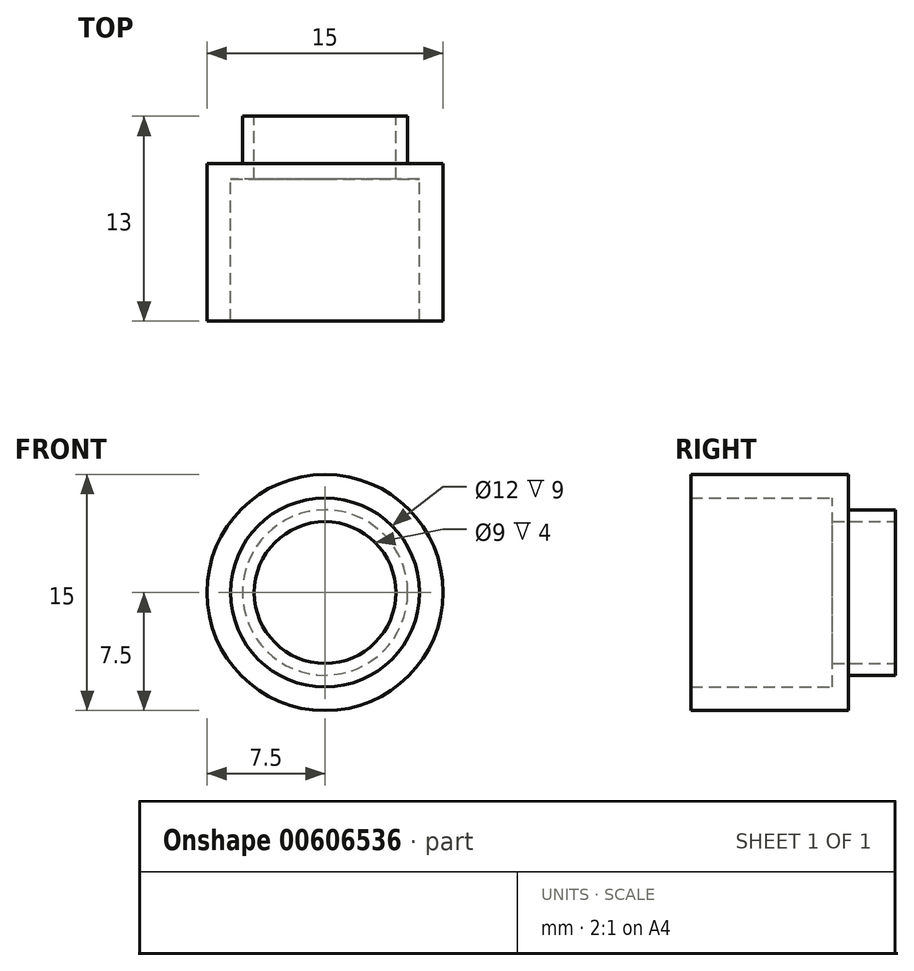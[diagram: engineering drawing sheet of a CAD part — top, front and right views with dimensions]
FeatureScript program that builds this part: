
annotation { "Feature Type Name" : "Feature", "Feature Type Description" : "" }
export const myFeature = defineFeature(function(context is Context, id is Id, definition is map)
    precondition{}
    {
        {
            var Q0;
            Q0=qCreatedBy(makeId("Front.planeOp"),FACE);
            var sketch = newSketch(context, id + "F0", { "sketchPlane" : qUnion([Q0])});
            skCircle(sketch, "E0", {"center": v(0, 0) * mm, "radius": 7.5 * mm});
            skCircle(sketch, "E1", {"center": v(0, 0) * mm, "radius": 6 * mm});
            skCircle(sketch, "E2", {"center": v(0, 0) * mm, "radius": 4.5 * mm});
            skCircle(sketch, "E3", {"center": v(0, 0) * mm, "radius": 5.25 * mm});
            skSolve(sketch);
        }
        {
            var Q0;
            Q0=makeQuery(id+"F0.imprint","IMPRINT",FACE,{"disambiguationData":[TD([[makeQuery(id+"F0.imprint","IMPRINT",EDGE,{"derivedFrom":sQuery(id+"F0.wireOp",EDGE,"E0")}),1.0]])]});
            extrude(context, id + "F1", {"entities" : qUnion([Q0]), "depth" : 10 * mm});
        }
        {
            var Q0;
            Q0=makeQuery(id+"F0.imprint","IMPRINT",FACE,{"disambiguationData":[TD([[makeQuery(id+"F0.imprint","IMPRINT",EDGE,{"derivedFrom":sQuery(id+"F0.wireOp",EDGE,"E1")}),1.0]])]});
            extrude(context, id + "F2", {"entities" : qUnion([Q0]), "operationType" : NewBodyOperationType.ADD, "depth" : 1 * mm});
        }
        {
            var Q0;
            Q0=makeQuery(id+"F0.imprint","IMPRINT",FACE,{"disambiguationData":[TD([[makeQuery(id+"F0.imprint","IMPRINT",EDGE,{"derivedFrom":sQuery(id+"F0.wireOp",EDGE,"E2")}),-1.0]])]});
            extrude(context, id + "F3", {"entities" : qUnion([Q0]), "operationType" : NewBodyOperationType.ADD, "depth" : 1 * mm, "hasSecondDirection" : true, "secondDirectionOppositeDirection" : true, "secondDirectionDepth" : 3 * mm});
        }
    });
